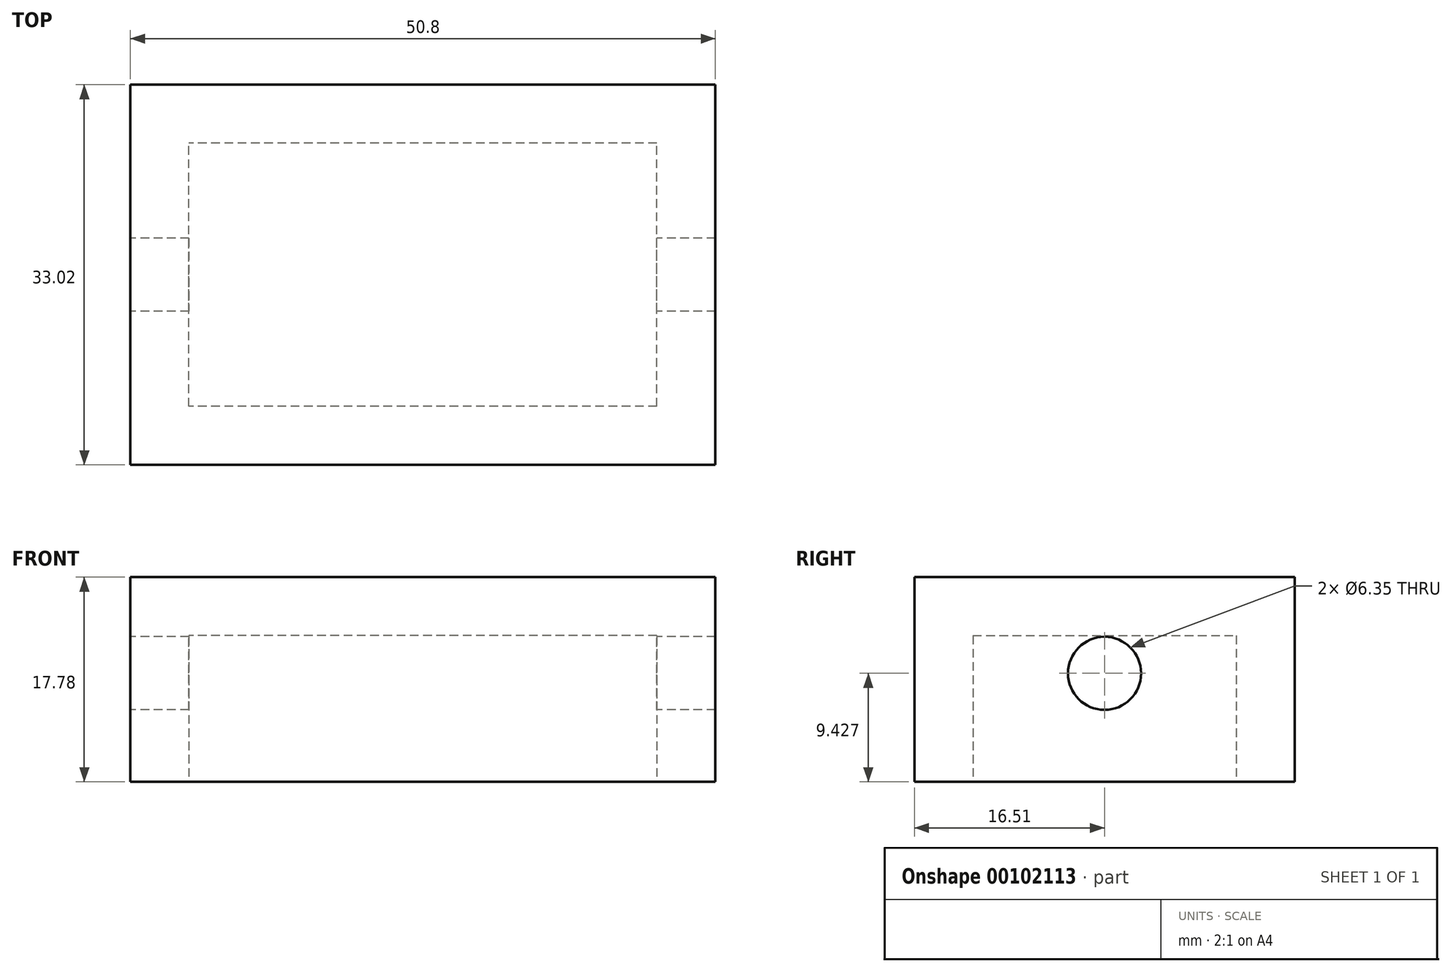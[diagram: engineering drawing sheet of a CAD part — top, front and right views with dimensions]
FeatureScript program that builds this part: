
annotation { "Feature Type Name" : "Feature", "Feature Type Description" : "" }
export const myFeature = defineFeature(function(context is Context, id is Id, definition is map)
    precondition{}
    {
        {
            var Q0;
            Q0=qCreatedBy(makeId("Top.planeOp"),FACE);
            var sketch = newSketch(context, id + "F0", { "sketchPlane" : qUnion([Q0])});
            skLineSegment(sketch, "E0.bottom", {"start": v(17.8, -13.13) * mm, "end": v(-33, -13.13) * mm});
            skLineSegment(sketch, "E0.top", {"start": v(17.8, -46.15) * mm, "end": v(-33, -46.15) * mm});
            skLineSegment(sketch, "E0.left", {"start": v(17.8, -13.13) * mm, "end": v(17.8, -46.15) * mm});
            skLineSegment(sketch, "E0.right", {"start": v(-33, -13.13) * mm, "end": v(-33, -46.15) * mm});
            skLineSegment(sketch, "E1.bottom", {"start": v(12.73, -41.07) * mm, "end": v(-27.91, -41.07) * mm});
            skLineSegment(sketch, "E1.top", {"start": v(12.73, -18.21) * mm, "end": v(-27.91, -18.21) * mm});
            skLineSegment(sketch, "E1.left", {"start": v(12.73, -41.07) * mm, "end": v(12.73, -18.21) * mm});
            skLineSegment(sketch, "E1.right", {"start": v(-27.91, -41.07) * mm, "end": v(-27.91, -18.21) * mm});
            skSolve(sketch);
        }
        {
            var Q0;
            Q0=makeQuery(id+"F0.imprint","IMPRINT",FACE,{"disambiguationData":[TD([[makeQuery(id+"F0.imprint","IMPRINT",EDGE,{"derivedFrom":sQuery(id+"F0.wireOp",EDGE,"E1.bottom")}),-1.0]])]});
            var Q1;
            Q1=makeQuery(id+"F0.imprint","IMPRINT",FACE,{"disambiguationData":[TD([[makeQuery(id+"F0.imprint","IMPRINT",EDGE,{"derivedFrom":sQuery(id+"F0.wireOp",EDGE,"E0.bottom")}),1.0]])]});
            extrude(context, id + "F1", {"entities" : qUnion([Q0, Q1]), "depth" : 17.78 * mm});
        }
        {
            var Q0;
            Q0=makeQuery(id+"F0.imprint","IMPRINT",FACE,{"disambiguationData":[TD([[makeQuery(id+"F0.imprint","IMPRINT",EDGE,{"derivedFrom":sQuery(id+"F0.wireOp",EDGE,"E1.bottom")}),-1.0]])]});
            extrude(context, id + "F2", {"entities" : qUnion([Q0]), "operationType" : NewBodyOperationType.REMOVE, "depth" : 12.7 * mm});
        }
        {
            var Q0;
            Q0=makeQuery(id+"F1.opExtrude","SWEPT_FACE",FACE,{"disambiguationData":[OSD([sQuery(id+"F0.wireOp",EDGE,"E0.right")])]});
            var sketch = newSketch(context, id + "F3", { "sketchPlane" : qUnion([Q0])});
            skCircle(sketch, "E2", {"center": v(29.64, 9.43) * mm, "radius": 3.17 * mm});
            skSolve(sketch);
        }
        {
            var Q0;
            Q0 = qSketchRegion(id + "F3", true);
            extrude(context, id + "F4", {"entities" : qUnion([Q0]), "operationType" : NewBodyOperationType.REMOVE, "oppositeDirection" : true, "depth" : 254 * mm});
        }
    });
